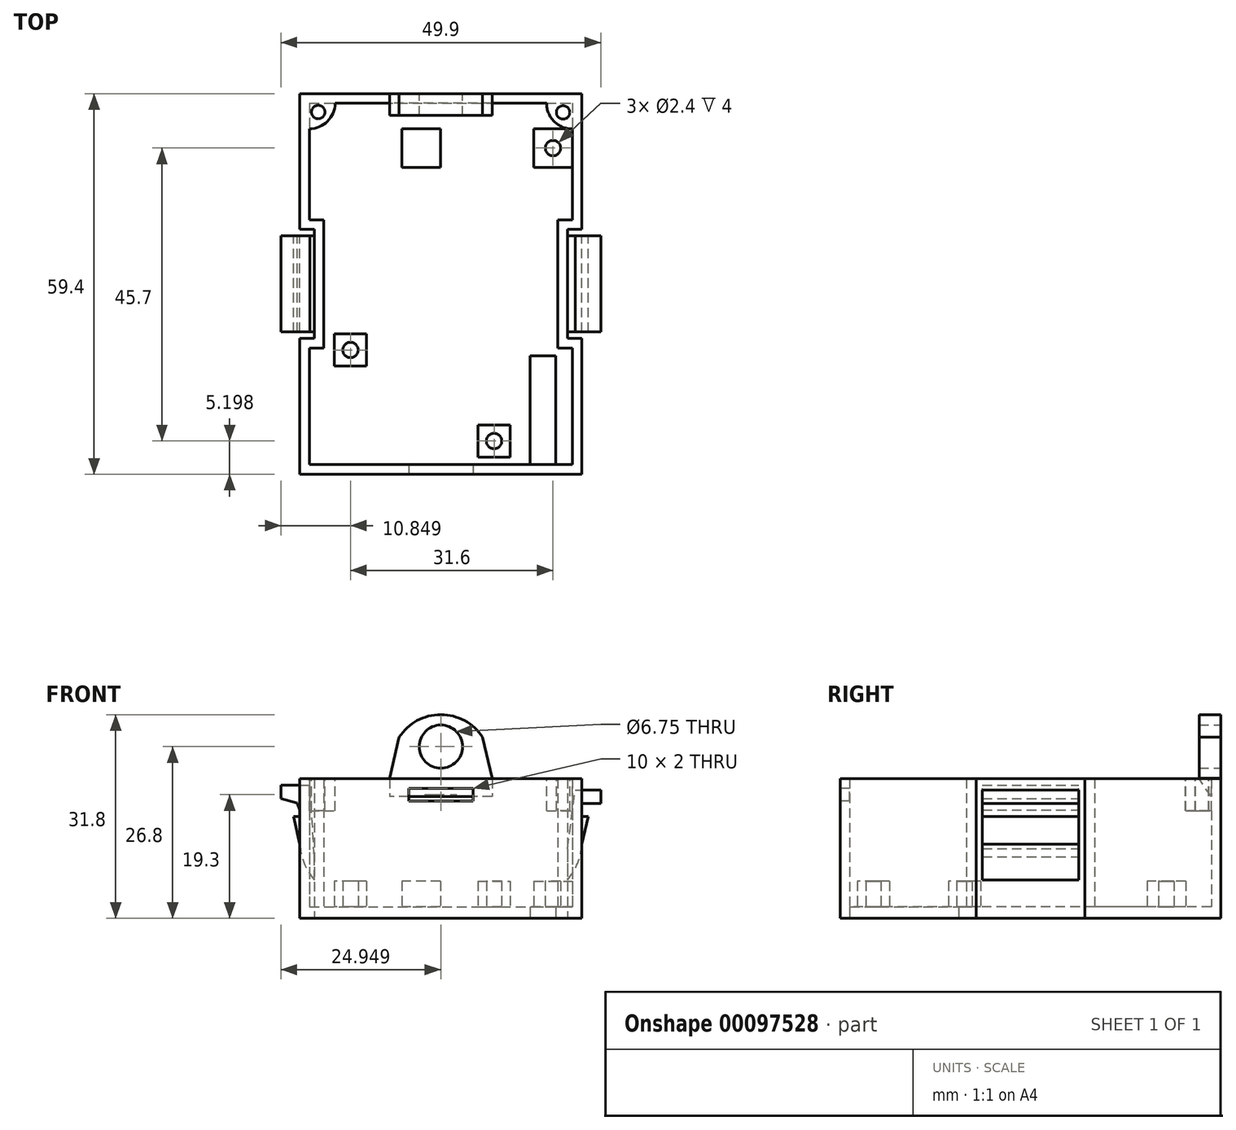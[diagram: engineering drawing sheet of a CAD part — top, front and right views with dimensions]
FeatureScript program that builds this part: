
annotation { "Feature Type Name" : "Feature", "Feature Type Description" : "" }
export const myFeature = defineFeature(function(context is Context, id is Id, definition is map)
    precondition{}
    {
        {
            var Q0;
            Q0=qCreatedBy(makeId("Top.planeOp"),FACE);
            var sketch = newSketch(context, id + "F0", { "sketchPlane" : qUnion([Q0])});
            skLineSegment(sketch, "E0.bottom", {"start": v(-56.63, 54.28) * mm, "end": v(-12.63, 54.28) * mm});
            skLineSegment(sketch, "E0.top", {"start": v(-56.63, -5.12) * mm, "end": v(-12.63, -5.12) * mm});
            skCircle(sketch, "E1", {"center": v(-12.63, -5.12) * mm, "radius": 1.5 * mm, "construction": true});
            skCircle(sketch, "E2", {"center": v(-56.63, -5.12) * mm, "radius": 1.5 * mm, "construction": true});
            skLineSegment(sketch, "E3", {"start": v(-56.63, -3.62) * mm, "end": v(-12.63, -3.62) * mm, "construction": true});
            skCircle(sketch, "E4", {"center": v(-12.63, -3.62) * mm, "radius": 4.1 * mm, "construction": true});
            skLineSegment(sketch, "E5.bottom", {"start": v(-16.73, -3.62) * mm, "end": v(-20.73, -3.62) * mm});
            skLineSegment(sketch, "E5.top", {"start": v(-16.73, 13.38) * mm, "end": v(-20.73, 13.38) * mm});
            skLineSegment(sketch, "E5.left", {"start": v(-16.73, -3.62) * mm, "end": v(-16.73, 13.38) * mm});
            skLineSegment(sketch, "E5.right", {"start": v(-20.73, -3.62) * mm, "end": v(-20.73, 13.38) * mm});
            skLineSegment(sketch, "E6", {"start": v(-56.63, 24.58) * mm, "end": v(-12.63, 24.58) * mm, "construction": true});
            skCircle(sketch, "E7", {"center": v(-56.63, 24.58) * mm, "radius": 8.5 * mm, "construction": true});
            skLineSegment(sketch, "E8", {"start": v(-56.63, 33.08) * mm, "end": v(-54.38, 33.08) * mm});
            skLineSegment(sketch, "E9", {"start": v(-56.63, 16.08) * mm, "end": v(-54.38, 16.08) * mm});
            skLineSegment(sketch, "E10", {"start": v(-54.38, 33.08) * mm, "end": v(-54.38, 16.08) * mm});
            skLineSegment(sketch, "E11", {"start": v(-56.63, 54.28) * mm, "end": v(-56.63, 33.08) * mm});
            skLineSegment(sketch, "E12", {"start": v(-56.63, 16.08) * mm, "end": v(-56.63, -5.12) * mm});
            skLineSegment(sketch, "E13", {"start": v(-34.63, 54.28) * mm, "end": v(-34.63, 40.65) * mm, "construction": true});
            skLineSegment(sketch, "E14.MirrorCS", {"start": v(-12.63, 16.08) * mm, "end": v(-12.63, -5.12) * mm});
            skLineSegment(sketch, "E15.MirrorCS", {"start": v(-12.63, 16.08) * mm, "end": v(-14.88, 16.08) * mm});
            skLineSegment(sketch, "E16.MirrorCS", {"start": v(-12.63, 33.08) * mm, "end": v(-14.88, 33.08) * mm});
            skLineSegment(sketch, "E17.MirrorCS", {"start": v(-12.63, 54.28) * mm, "end": v(-12.63, 33.08) * mm});
            skLineSegment(sketch, "E18.MirrorCS", {"start": v(-14.88, 33.08) * mm, "end": v(-14.88, 16.08) * mm});
            skSolve(sketch);
        }
        {
            var Q0;
            Q0=makeQuery(id+"F0.imprint","IMPRINT",FACE,{"disambiguationData":[TD([[makeQuery(id+"F0.imprint","IMPRINT",EDGE,{"derivedFrom":sQuery(id+"F0.wireOp",EDGE,"E0.bottom")}),-1.0]])]});
            extrude(context, id + "F1", {"entities" : qUnion([Q0]), "depth" : 1.8 * mm});
        }
        {
            var Q0;
            Q0=makeQuery(id+"F1.opExtrude","CAP_FACE",FACE,{"disambiguationData":[OSD([sQuery(id+"F0.wireOp",EDGE,"E0.bottom"),sQuery(id+"F0.wireOp",EDGE,"E0.top"),sQuery(id+"F0.wireOp",EDGE,"E5.bottom"),sQuery(id+"F0.wireOp",EDGE,"E5.top"),sQuery(id+"F0.wireOp",EDGE,"E5.left"),sQuery(id+"F0.wireOp",EDGE,"E5.right"),sQuery(id+"F0.wireOp",EDGE,"E8"),sQuery(id+"F0.wireOp",EDGE,"E9"),sQuery(id+"F0.wireOp",EDGE,"E10"),sQuery(id+"F0.wireOp",EDGE,"E11"),sQuery(id+"F0.wireOp",EDGE,"E12"),sQuery(id+"F0.wireOp",EDGE,"E14.MirrorCS"),sQuery(id+"F0.wireOp",EDGE,"E15.MirrorCS"),sQuery(id+"F0.wireOp",EDGE,"E16.MirrorCS"),sQuery(id+"F0.wireOp",EDGE,"E17.MirrorCS"),sQuery(id+"F0.wireOp",EDGE,"E18.MirrorCS")])],"isStart":false});
            var sketch = newSketch(context, id + "F2", { "sketchPlane" : qUnion([Q0])});
            skLineSegment(sketch, "E19.0", {"start": v(-55.13, 52.78) * mm, "end": v(-55.13, 34.58) * mm});
            skLineSegment(sketch, "E19.1", {"start": v(-14.13, 14.58) * mm, "end": v(-16.38, 14.58) * mm});
            skLineSegment(sketch, "E19.2", {"start": v(-16.38, 34.58) * mm, "end": v(-16.38, 14.58) * mm});
            skLineSegment(sketch, "E19.3", {"start": v(-14.13, 34.58) * mm, "end": v(-16.38, 34.58) * mm});
            skLineSegment(sketch, "E19.4", {"start": v(-14.13, 52.78) * mm, "end": v(-14.13, 34.58) * mm});
            skLineSegment(sketch, "E19.5", {"start": v(-14.13, 14.58) * mm, "end": v(-14.13, -3.62) * mm});
            skLineSegment(sketch, "E19.6", {"start": v(-55.13, 52.78) * mm, "end": v(-14.13, 52.78) * mm});
            skLineSegment(sketch, "E19.7", {"start": v(-55.13, -3.62) * mm, "end": v(-14.13, -3.62) * mm});
            skLineSegment(sketch, "E19.8", {"start": v(-55.13, 14.58) * mm, "end": v(-55.13, -3.62) * mm});
            skLineSegment(sketch, "E19.9", {"start": v(-55.13, 14.58) * mm, "end": v(-52.88, 14.58) * mm});
            skLineSegment(sketch, "E19.10", {"start": v(-52.88, 34.58) * mm, "end": v(-52.88, 14.58) * mm});
            skLineSegment(sketch, "E19.11", {"start": v(-55.13, 34.58) * mm, "end": v(-52.88, 34.58) * mm});
            skSolve(sketch);
        }
        {
            var Q0;
            Q0=makeQuery(id+"F2.imprint","IMPRINT",FACE,{"disambiguationData":[TD([[makeQuery(id+"F2.imprint","IMPRINT",EDGE,{"derivedFrom":sQuery(id+"F2.wireOp",EDGE,"E19.0")}),-1.0]])]});
            extrude(context, id + "F3", {"entities" : qUnion([Q0]), "operationType" : NewBodyOperationType.ADD, "depth" : 20 * mm});
        }
        {
            var Q0;
            {var subQ0=sQuery(id+"F0.wireOp",EDGE,"E8");Q0=makeQuery(id+"F3.boolean.opBoolean","MERGE",FACE,{"derivedFrom":[makeQuery(id+"F1.opExtrude","SWEPT_FACE",FACE,{"disambiguationData":[OSD([subQ0])]}),makeQuery(id+"F3.opExtrude","SWEPT_FACE",FACE,{"disambiguationData":[OSD([subQ0])]})]});}
            var sketch = newSketch(context, id + "F4", { "sketchPlane" : qUnion([Q0])});
            skLineSegment(sketch, "E20", {"start": v(-56.63, 21.8) * mm, "end": v(-54.38, 21.8) * mm});
            skLineSegment(sketch, "E21", {"start": v(-56.63, 21.8) * mm, "end": v(-56.63, 22.8) * mm});
            skLineSegment(sketch, "E22", {"start": v(-56.63, 21.8) * mm, "end": v(-55.5, 21.8) * mm});
            skCircle(sketch, "E23", {"center": v(-56.63, 21.8) * mm, "radius": 2 * mm, "construction": true});
            skLineSegment(sketch, "E24", {"start": v(-56.63, 22.8) * mm, "end": v(-54.38, 21.8) * mm});
            skSolve(sketch);
        }
        {
            var Q0;
            Q0=qSketchRegion(id+"F4",true);
            extrude(context, id + "F5", {"entities" : qUnion([Q0]), "operationType" : NewBodyOperationType.REMOVE, "depth" : 17 * mm});
        }
        {
            var Q0;
            {var subQ0=sQuery(id+"F0.wireOp",EDGE,"E15.MirrorCS");Q0=makeQuery(id+"F3.boolean.opBoolean","MERGE",FACE,{"derivedFrom":[makeQuery(id+"F1.opExtrude","SWEPT_FACE",FACE,{"disambiguationData":[OSD([subQ0])]}),makeQuery(id+"F3.opExtrude","SWEPT_FACE",FACE,{"disambiguationData":[OSD([subQ0])]})]});}
            var sketch = newSketch(context, id + "F6", { "sketchPlane" : qUnion([Q0])});
            skLineSegment(sketch, "E25", {"start": v(12.63, 21.8) * mm, "end": v(12.63, 22.8) * mm});
            skLineSegment(sketch, "E26", {"start": v(12.63, 22.8) * mm, "end": v(14.88, 21.8) * mm});
            skLineSegment(sketch, "E27", {"start": v(14.88, 21.8) * mm, "end": v(12.63, 21.8) * mm});
            skSolve(sketch);
        }
        {
            var Q0;
            Q0=qSketchRegion(id+"F6",true);
            extrude(context, id + "F7", {"entities" : qUnion([Q0]), "operationType" : NewBodyOperationType.REMOVE, "depth" : 17 * mm});
        }
        {
            var Q0;
            {var subQ0=sQuery(id+"F0.wireOp",EDGE,"E0.top");Q0=makeQuery(id+"F6ghHVKL5EjysOi_1.boolean.opBoolean","MERGE",FACE,{"derivedFrom":[makeQuery(id+"F3.boolean.opBoolean","MERGE",FACE,{"derivedFrom":[makeQuery(id+"F1.opExtrude","SWEPT_FACE",FACE,{"disambiguationData":[OSD([subQ0])]}),makeQuery(id+"F3.opExtrude","SWEPT_FACE",FACE,{"disambiguationData":[OSD([subQ0])]})]}),makeQuery(id+"F6ghHVKL5EjysOi_1.opExtrude","SWEPT_FACE",FACE,{"disambiguationData":[OSD([sQuery(id+"FZ5MUIDVzBKq7bX_1.wireOp",EDGE,"YdwC2A8M-5GiA-6Idz-uFSA-seqV52Q8DN6U.top")])]})]});}
            var sketch = newSketch(context, id + "F8", { "sketchPlane" : qUnion([Q0])});
            skLineSegment(sketch, "E28.top", {"start": v(-29.63, 21.8) * mm, "end": v(-39.63, 21.8) * mm});
            skCircle(sketch, "E29", {"center": v(-56.63, 21.8) * mm, "radius": 1.5 * mm, "construction": true});
            skLineSegment(sketch, "E30", {"start": v(-56.63, 20.3) * mm, "end": v(-12.63, 20.3) * mm, "construction": true});
            skCircle(sketch, "E31", {"center": v(-34.63, 20.3) * mm, "radius": 5 * mm, "construction": true});
            skLineSegment(sketch, "E32", {"start": v(-39.63, 20.3) * mm, "end": v(-39.63, 18.3) * mm, "construction": true});
            skLineSegment(sketch, "E33.bottom", {"start": v(-39.63, 18.3) * mm, "end": v(-29.63, 18.3) * mm});
            skLineSegment(sketch, "E33.top", {"start": v(-39.63, 20.3) * mm, "end": v(-29.63, 20.3) * mm});
            skLineSegment(sketch, "E33.left", {"start": v(-39.63, 18.3) * mm, "end": v(-39.63, 20.3) * mm});
            skLineSegment(sketch, "E33.right", {"start": v(-29.63, 18.3) * mm, "end": v(-29.63, 20.3) * mm});
            skSolve(sketch);
        }
        {
            var Q0;
            Q0=qSketchRegion(id+"F8",true);
            extrude(context, id + "F9", {"entities" : qUnion([Q0]), "operationType" : NewBodyOperationType.REMOVE, "oppositeDirection" : true, "depth" : 2.5 * mm});
        }
        {
            var Q0;
            {var subQ0=sQuery(id+"F0.wireOp",EDGE,"E16.MirrorCS");Q0=makeQuery(id+"F7.boolean.opBoolean","MERGE",FACE,{"derivedFrom":[makeQuery(id+"F3.boolean.opBoolean","MERGE",FACE,{"derivedFrom":[makeQuery(id+"F1.opExtrude","SWEPT_FACE",FACE,{"disambiguationData":[OSD([subQ0])]}),makeQuery(id+"F3.opExtrude","SWEPT_FACE",FACE,{"disambiguationData":[OSD([subQ0])]})]}),makeQuery(id+"F7.opExtrude","CAP_FACE",FACE,{"disambiguationData":[OSD([sQuery(id+"F6.wireOp",EDGE,"E25"),sQuery(id+"F6.wireOp",EDGE,"E26"),sQuery(id+"F6.wireOp",EDGE,"E27")])],"isStart":false})]});}
            var sketch = newSketch(context, id + "F10", { "sketchPlane" : qUnion([Q0])});
            skLineSegment(sketch, "E34", {"start": v(-14.88, 0) * mm, "end": v(-14.88, 6) * mm, "construction": true});
            skCircle(sketch, "E35", {"center": v(-14.88, 6) * mm, "radius": 6 * mm, "construction": true});
            skArc(sketch, "E36", {"start": v(-14.88, 6) * mm, "mid": v(-13.3, 8.6) * mm, "end": v(-12.63, 11.56) * mm});
            skCircle(sketch, "E37", {"center": v(-14.88, 10.9) * mm, "radius": 5 * mm, "construction": true});
            skLineSegment(sketch, "E38", {"start": v(-14.88, 15.9) * mm, "end": v(-5.95, 15.9) * mm, "construction": true});
            skCircle(sketch, "E39", {"center": v(-12.63, 15.9) * mm, "radius": 1 * mm, "construction": true});
            skLineSegment(sketch, "E40", {"start": v(-12.63, 11.56) * mm, "end": v(-11.63, 15.9) * mm});
            skCircle(sketch, "E41", {"center": v(-14.88, 15.9) * mm, "radius": 1.2 * mm, "construction": true});
            skLineSegment(sketch, "E42", {"start": v(-13.68, 20) * mm, "end": v(-9.68, 20) * mm});
            skLineSegment(sketch, "E43", {"start": v(-11.63, 15.9) * mm, "end": v(-12.63, 15.9) * mm});
            skCircle(sketch, "E44", {"center": v(-12.63, 15.9) * mm, "radius": 2 * mm, "construction": true});
            skLineSegment(sketch, "E45", {"start": v(-12.63, 15.9) * mm, "end": v(-12.63, 17.9) * mm});
            skLineSegment(sketch, "E46", {"start": v(-12.63, 17.9) * mm, "end": v(-9.68, 17.9) * mm});
            skLineSegment(sketch, "E47", {"start": v(-14.88, 10.9) * mm, "end": v(-13.68, 20) * mm});
            skLineSegment(sketch, "E48", {"start": v(-9.68, 20) * mm, "end": v(-9.68, 17.9) * mm});
            skLineSegment(sketch, "E49", {"start": v(-12.63, 6.02) * mm, "end": v(-56.63, 6.02) * mm, "construction": true});
            skLineSegment(sketch, "E50", {"start": v(-34.63, 6.02) * mm, "end": v(-34.63, 12.32) * mm, "construction": true});
            skCircle(sketch, "E51.MirrorC", {"center": v(-56.63, 15.9) * mm, "radius": 2 * mm, "construction": true});
            skLineSegment(sketch, "E52.MirrorCS", {"start": v(-56.63, 11.56) * mm, "end": v(-57.63, 15.9) * mm});
            skArc(sketch, "E53.MirrorCS", {"start": v(-54.38, 6) * mm, "mid": v(-55.96, 8.6) * mm, "end": v(-56.63, 11.56) * mm});
            skLineSegment(sketch, "E54.MirrorCS", {"start": v(-57.63, 15.9) * mm, "end": v(-56.63, 15.9) * mm});
            skLineSegment(sketch, "E55", {"start": v(-14.88, 10.9) * mm, "end": v(-14.88, 6) * mm});
            skCircle(sketch, "E56", {"center": v(-56.63, 17.9) * mm, "radius": 0.8 * mm, "construction": true});
            skPoint(sketch, "E57.endSnap0", {"position": v(-56.63, 16.9) * mm});
            skLineSegment(sketch, "E58", {"start": v(-56.63, 18.7) * mm, "end": v(-59.88, 18.7) * mm, "construction": true});
            skLineSegment(sketch, "E59", {"start": v(-59.58, 18.7) * mm, "end": v(-59.58, 20.8) * mm});
            skLineSegment(sketch, "E60", {"start": v(-59.58, 18.7) * mm, "end": v(-57.03, 18) * mm});
            skLineSegment(sketch, "E61", {"start": v(-56.63, 15.9) * mm, "end": v(-56.63, 16.9) * mm});
            skLineSegment(sketch, "E62", {"start": v(-56.63, 16.9) * mm, "end": v(-57.03, 18) * mm});
            skLineSegment(sketch, "E63", {"start": v(-59.58, 20.8) * mm, "end": v(-55.04, 20.8) * mm});
            skLineSegment(sketch, "E64", {"start": v(-54.38, 6) * mm, "end": v(-54.38, 9.6) * mm});
            skLineSegment(sketch, "E65", {"start": v(-54.38, 9.6) * mm, "end": v(-55.04, 20.8) * mm});
            skSolve(sketch);
        }
        {
            var Q0;
            Q0=makeQuery(id+"F10.imprint","IMPRINT",FACE,{"disambiguationData":[TD([[makeQuery(id+"F10.imprint","IMPRINT",EDGE,{"derivedFrom":sQuery(id+"F10.wireOp",EDGE,"3a5f83b2-c532-4f29-86cb-ad45a0fee2c30.MirrorCS")}),1.0]])]});
            var Q1;
            {var subQ6=sQuery(id+"F10.wireOp",EDGE,"E46");Q1=makeQuery(id+"F10.imprint","IMPRINT",FACE,{"disambiguationData":[TD([[makeQuery(id+"F10.imprint","IMPRINT",EDGE,{"derivedFrom":subQ6}),1.0]])]});}
            var Q2;
            {var subQ7=sQuery(id+"F10.wireOp",EDGE,"E36");Q2=makeQuery(id+"F10.imprint","IMPRINT",FACE,{"disambiguationData":[TD([[makeQuery(id+"F10.imprint","IMPRINT",EDGE,{"derivedFrom":subQ7}),1.0]])]});}
            var Q3;
            {var subQ0=sQuery(id+"F10.wireOp",EDGE,"E40");Q3=makeQuery(id+"F10.imprint","IMPRINT",FACE,{"disambiguationData":[TD([[makeQuery(id+"F10.imprint","IMPRINT",EDGE,{"derivedFrom":subQ0}),1.0]])]});}
            var Q4;
            Q4=makeQuery(id+"F10.imprint","IMPRINT",FACE,{"disambiguationData":[TD([[makeQuery(id+"F10.imprint","IMPRINT",EDGE,{"derivedFrom":sQuery(id+"F10.wireOp",EDGE,"E52.MirrorCS")}),-1.0]])]});
            extrude(context, id + "F11", {"entities" : qUnion([Q0, Q1, Q2, Q3, Q4]), "operationType" : NewBodyOperationType.ADD, "depth" : 16 * mm, "hasSecondDirection" : true, "secondDirectionOppositeDirection" : false, "secondDirectionDepth" : 1 * mm});
        }
        {
            var Q0;
            Q0=makeQuery(id+"F1.opExtrude","CAP_FACE",FACE,{"disambiguationData":[OSD([sQuery(id+"F0.wireOp",EDGE,"E0.bottom"),sQuery(id+"F0.wireOp",EDGE,"E0.top"),sQuery(id+"F0.wireOp",EDGE,"E5.bottom"),sQuery(id+"F0.wireOp",EDGE,"E5.top"),sQuery(id+"F0.wireOp",EDGE,"E5.left"),sQuery(id+"F0.wireOp",EDGE,"E5.right"),sQuery(id+"F0.wireOp",EDGE,"E8"),sQuery(id+"F0.wireOp",EDGE,"E9"),sQuery(id+"F0.wireOp",EDGE,"E10"),sQuery(id+"F0.wireOp",EDGE,"E11"),sQuery(id+"F0.wireOp",EDGE,"E12"),sQuery(id+"F0.wireOp",EDGE,"E14.MirrorCS"),sQuery(id+"F0.wireOp",EDGE,"E15.MirrorCS"),sQuery(id+"F0.wireOp",EDGE,"E16.MirrorCS"),sQuery(id+"F0.wireOp",EDGE,"E17.MirrorCS"),sQuery(id+"F0.wireOp",EDGE,"E18.MirrorCS")])],"isStart":false});
            var sketch = newSketch(context, id + "F12", { "sketchPlane" : qUnion([Q0])});
            skCircle(sketch, "E66", {"center": v(-14.13, 34.58) * mm, "radius": 3 * mm, "construction": true});
            skLineSegment(sketch, "E67", {"start": v(-14.13, 34.58) * mm, "end": v(-19.1, 34.58) * mm, "construction": true});
            skLineSegment(sketch, "E68", {"start": v(-17.13, 34.58) * mm, "end": v(-17.13, 52.78) * mm, "construction": true});
            skCircle(sketch, "E69", {"center": v(-17.13, 52.78) * mm, "radius": 7 * mm, "construction": true});
            skCircle(sketch, "E70", {"center": v(-17.13, 45.78) * mm, "radius": 3 * mm, "construction": true});
            skCircle(sketch, "E71", {"center": v(-17.13, 45.78) * mm, "radius": 1.2 * mm});
            skLineSegment(sketch, "E72.bottom", {"start": v(-20.13, 48.78) * mm, "end": v(-14.13, 48.78) * mm});
            skLineSegment(sketch, "E72.top", {"start": v(-20.13, 42.78) * mm, "end": v(-14.13, 42.78) * mm});
            skLineSegment(sketch, "E72.left", {"start": v(-20.13, 48.78) * mm, "end": v(-20.13, 42.78) * mm});
            skLineSegment(sketch, "E72.right", {"start": v(-14.13, 48.78) * mm, "end": v(-14.13, 42.78) * mm});
            skLineSegment(sketch, "E73", {"start": v(-49.88, -3.62) * mm, "end": v(-49.88, 0.08) * mm, "construction": true});
            skLineSegment(sketch, "E74", {"start": v(-49.88, 0.08) * mm, "end": v(-11.04, 0.08) * mm, "construction": true});
            skCircle(sketch, "E75", {"center": v(-14.13, 0.08) * mm, "radius": 12.2 * mm, "construction": true});
            skCircle(sketch, "E76", {"center": v(-26.33, 0.08) * mm, "radius": 1.2 * mm});
            skLineSegment(sketch, "E77.bottom", {"start": v(-28.83, 2.58) * mm, "end": v(-23.83, 2.58) * mm});
            skLineSegment(sketch, "E77.top", {"start": v(-28.83, -2.42) * mm, "end": v(-23.83, -2.42) * mm});
            skLineSegment(sketch, "E77.left", {"start": v(-28.83, 2.58) * mm, "end": v(-28.83, -2.42) * mm});
            skLineSegment(sketch, "E77.right", {"start": v(-23.83, 2.58) * mm, "end": v(-23.83, -2.42) * mm});
            skLineSegment(sketch, "E78", {"start": v(-55.13, -2.16) * mm, "end": v(-48.73, -2.16) * mm, "construction": true});
            skLineSegment(sketch, "E79", {"start": v(-48.73, -2.16) * mm, "end": v(-48.73, 60.43) * mm, "construction": true});
            skLineSegment(sketch, "E80", {"start": v(-48.73, -2.16) * mm, "end": v(-48.73, -6.57) * mm, "construction": true});
            skCircle(sketch, "E81", {"center": v(-48.73, -3.62) * mm, "radius": 17.9 * mm, "construction": true});
            skCircle(sketch, "E82", {"center": v(-48.73, 14.28) * mm, "radius": 1.2 * mm});
            skLineSegment(sketch, "E83.bottom", {"start": v(-46.23, 16.78) * mm, "end": v(-51.23, 16.78) * mm});
            skLineSegment(sketch, "E83.top", {"start": v(-46.23, 11.78) * mm, "end": v(-51.23, 11.78) * mm});
            skLineSegment(sketch, "E83.left", {"start": v(-46.23, 16.78) * mm, "end": v(-46.23, 11.78) * mm});
            skLineSegment(sketch, "E83.right", {"start": v(-51.23, 16.78) * mm, "end": v(-51.23, 11.78) * mm});
            skLineSegment(sketch, "E84", {"start": v(-17.13, 45.78) * mm, "end": v(-37.7, 45.78) * mm, "construction": true});
            skLineSegment(sketch, "E85.bottom", {"start": v(-34.7, 48.78) * mm, "end": v(-40.7, 48.78) * mm});
            skLineSegment(sketch, "E85.top", {"start": v(-34.7, 42.78) * mm, "end": v(-40.7, 42.78) * mm});
            skLineSegment(sketch, "E85.left", {"start": v(-34.7, 48.78) * mm, "end": v(-34.7, 42.78) * mm});
            skLineSegment(sketch, "E85.right", {"start": v(-40.7, 48.78) * mm, "end": v(-40.7, 42.78) * mm});
            skPoint(sketch, "E85.middle", {"position": v(-37.7, 45.78) * mm});
            skSolve(sketch);
        }
        {
            var Q0;
            Q0=makeQuery(id+"F12.imprint","IMPRINT",FACE,{"disambiguationData":[TD([[makeQuery(id+"F12.imprint","IMPRINT",EDGE,{"derivedFrom":sQuery(id+"F12.wireOp",EDGE,"E82")}),-1.0]])]});
            var Q1;
            Q1=makeQuery(id+"F12.imprint","IMPRINT",FACE,{"disambiguationData":[TD([[makeQuery(id+"F12.imprint","IMPRINT",EDGE,{"derivedFrom":sQuery(id+"F12.wireOp",EDGE,"E76")}),-1.0]])]});
            var Q2;
            Q2=makeQuery(id+"F12.imprint","IMPRINT",FACE,{"disambiguationData":[TD([[makeQuery(id+"F12.imprint","IMPRINT",EDGE,{"derivedFrom":sQuery(id+"F12.wireOp",EDGE,"E71")}),-1.0]])]});
            var Q3;
            Q3=makeQuery(id+"F12.imprint","IMPRINT",FACE,{"disambiguationData":[TD([[makeQuery(id+"F12.imprint","IMPRINT",EDGE,{"derivedFrom":sQuery(id+"F12.wireOp",EDGE,"E85.bottom")}),1.0]])]});
            extrude(context, id + "F13", {"entities" : qUnion([Q0, Q1, Q2, Q3]), "operationType" : NewBodyOperationType.ADD, "depth" : 4 * mm});
        }
        {
            var Q0;
            Q0=makeQuery(id+"F3.opExtrude","CAP_FACE",FACE,{"disambiguationData":[OSD([sQuery(id+"F0.wireOp",EDGE,"E0.bottom"),sQuery(id+"F0.wireOp",EDGE,"E0.top"),sQuery(id+"F0.wireOp",EDGE,"E8"),sQuery(id+"F0.wireOp",EDGE,"E9"),sQuery(id+"F0.wireOp",EDGE,"E10"),sQuery(id+"F0.wireOp",EDGE,"E11"),sQuery(id+"F0.wireOp",EDGE,"E12"),sQuery(id+"F0.wireOp",EDGE,"E14.MirrorCS"),sQuery(id+"F0.wireOp",EDGE,"E15.MirrorCS"),sQuery(id+"F0.wireOp",EDGE,"E16.MirrorCS"),sQuery(id+"F0.wireOp",EDGE,"E17.MirrorCS"),sQuery(id+"F0.wireOp",EDGE,"E18.MirrorCS"),sQuery(id+"F2.wireOp",EDGE,"E19.0"),sQuery(id+"F2.wireOp",EDGE,"E19.1"),sQuery(id+"F2.wireOp",EDGE,"E19.2"),sQuery(id+"F2.wireOp",EDGE,"E19.3"),sQuery(id+"F2.wireOp",EDGE,"E19.4"),sQuery(id+"F2.wireOp",EDGE,"E19.5"),sQuery(id+"F2.wireOp",EDGE,"E19.6"),sQuery(id+"F2.wireOp",EDGE,"E19.7"),sQuery(id+"F2.wireOp",EDGE,"E19.8"),sQuery(id+"F2.wireOp",EDGE,"E19.9"),sQuery(id+"F2.wireOp",EDGE,"E19.10"),sQuery(id+"F2.wireOp",EDGE,"E19.11")])],"isStart":false});
            var sketch = newSketch(context, id + "F14", { "sketchPlane" : qUnion([Q0])});
            skCircle(sketch, "E86", {"center": v(-55.13, 52.78) * mm, "radius": 4 * mm, "construction": true});
            skArc(sketch, "E87", {"start": v(-55.13, 48.78) * mm, "mid": v(-52.32, 49.97) * mm, "end": v(-51.13, 52.78) * mm});
            skLineSegment(sketch, "E88", {"start": v(-55.19, 52.83) * mm, "end": v(-52.32, 49.97) * mm, "construction": true});
            skCircle(sketch, "E89", {"center": v(-53.75, 51.4) * mm, "radius": 1.05 * mm});
            skCircle(sketch, "E90", {"center": v(-14.13, 52.78) * mm, "radius": 4 * mm, "construction": true});
            skArc(sketch, "E91", {"start": v(-18.13, 52.78) * mm, "mid": v(-16.97, 49.94) * mm, "end": v(-14.13, 48.78) * mm});
            skLineSegment(sketch, "E92", {"start": v(-14.16, 52.75) * mm, "end": v(-16.97, 49.94) * mm, "construction": true});
            skCircle(sketch, "E93", {"center": v(-15.56, 51.35) * mm, "radius": 1.05 * mm});
            skLineSegment(sketch, "E94", {"start": v(-55.13, 48.78) * mm, "end": v(-55.13, 52.78) * mm});
            skLineSegment(sketch, "E95", {"start": v(-18.13, 52.78) * mm, "end": v(-14.13, 52.78) * mm});
            skLineSegment(sketch, "E96", {"start": v(-51.13, 52.78) * mm, "end": v(-18.13, 52.78) * mm});
            skLineSegment(sketch, "E97", {"start": v(-14.13, 48.78) * mm, "end": v(-14.13, 34.58) * mm});
            skLineSegment(sketch, "E98", {"start": v(-14.13, 34.58) * mm, "end": v(-16.38, 34.58) * mm});
            skLineSegment(sketch, "E99", {"start": v(-16.38, 34.58) * mm, "end": v(-16.38, 14.58) * mm});
            skLineSegment(sketch, "E100", {"start": v(-16.38, 14.58) * mm, "end": v(-14.13, 14.58) * mm});
            skLineSegment(sketch, "E101", {"start": v(-14.13, 14.58) * mm, "end": v(-14.13, -3.62) * mm});
            skLineSegment(sketch, "E102", {"start": v(-14.13, -3.62) * mm, "end": v(-55.13, -3.62) * mm});
            skLineSegment(sketch, "E103", {"start": v(-55.13, -3.62) * mm, "end": v(-55.13, 14.58) * mm});
            skLineSegment(sketch, "E104", {"start": v(-55.13, 14.58) * mm, "end": v(-52.88, 14.58) * mm});
            skLineSegment(sketch, "E105", {"start": v(-52.88, 14.58) * mm, "end": v(-52.88, 34.58) * mm});
            skLineSegment(sketch, "E106", {"start": v(-52.88, 34.58) * mm, "end": v(-55.13, 34.58) * mm});
            skLineSegment(sketch, "E107", {"start": v(-55.13, 34.58) * mm, "end": v(-55.13, 48.78) * mm});
            skLineSegment(sketch, "E108", {"start": v(-51.13, 52.78) * mm, "end": v(-55.13, 52.78) * mm});
            skSolve(sketch);
        }
        {
            var Q0;
            Q0=makeQuery(id+"F14.imprint","IMPRINT",FACE,{"disambiguationData":[TD([[makeQuery(id+"F14.imprint","IMPRINT",EDGE,{"derivedFrom":sQuery(id+"F14.wireOp",EDGE,"E93")}),-1.0]])]});
            var Q1;
            Q1=makeQuery(id+"F14.imprint","IMPRINT",FACE,{"disambiguationData":[TD([[makeQuery(id+"F14.imprint","IMPRINT",EDGE,{"derivedFrom":sQuery(id+"F14.wireOp",EDGE,"E89")}),-1.0]])]});
            extrude(context, id + "F15", {"entities" : qUnion([Q0, Q1]), "operationType" : NewBodyOperationType.ADD, "oppositeDirection" : true, "depth" : 5 * mm});
        }
        {
            var Q0;
            {var subQ0=sQuery(id+"F0.wireOp",EDGE,"E0.bottom");Q0=makeQuery(id+"F3.boolean.opBoolean","MERGE",FACE,{"derivedFrom":[makeQuery(id+"F1.opExtrude","SWEPT_FACE",FACE,{"disambiguationData":[OSD([subQ0])]}),makeQuery(id+"F3.opExtrude","SWEPT_FACE",FACE,{"disambiguationData":[OSD([subQ0])]})]});}
            var sketch = newSketch(context, id + "F16", { "sketchPlane" : qUnion([Q0])});
            skLineSegment(sketch, "E109", {"start": v(34.63, 21.8) * mm, "end": v(34.63, 31.8) * mm, "construction": true});
            skCircle(sketch, "E110", {"center": v(34.63, 26.8) * mm, "radius": 3.38 * mm});
            skCircle(sketch, "E111", {"center": v(34.63, 26.8) * mm, "radius": 5 * mm, "construction": true});
            skLineSegment(sketch, "E112", {"start": v(29.85, 28.25) * mm, "end": v(39.42, 28.25) * mm, "construction": true});
            skArc(sketch, "E113", {"start": v(39.42, 28.25) * mm, "mid": v(34.63, 31.8) * mm, "end": v(29.85, 28.25) * mm});
            skLineSegment(sketch, "E114", {"start": v(34.63, 28.25) * mm, "end": v(28.13, 28.25) * mm, "construction": true});
            skLineSegment(sketch, "E115", {"start": v(34.63, 28.25) * mm, "end": v(41.13, 28.25) * mm, "construction": true});
            skArc(sketch, "E116", {"start": v(41.13, 28.25) * mm, "mid": v(34.63, 31.8) * mm, "end": v(28.13, 28.25) * mm});
            skCircle(sketch, "E117", {"center": v(34.63, 21.8) * mm, "radius": 8 * mm, "construction": true});
            skLineSegment(sketch, "E118", {"start": v(42.63, 21.8) * mm, "end": v(42.63, 21.9) * mm});
            skLineSegment(sketch, "E119", {"start": v(26.63, 21.8) * mm, "end": v(26.63, 21.9) * mm});
            skLineSegment(sketch, "E120", {"start": v(26.63, 21.9) * mm, "end": v(28.13, 28.25) * mm});
            skLineSegment(sketch, "E121", {"start": v(42.63, 21.9) * mm, "end": v(41.13, 28.25) * mm});
            skSolve(sketch);
        }
        {
            var Q0;
            Q0=makeQuery(id+"F16.imprint","IMPRINT",FACE,{"disambiguationData":[TD([[makeQuery(id+"F16.imprint","IMPRINT",EDGE,{"derivedFrom":sQuery(id+"F16.wireOp",EDGE,"E110")}),-1.0]])]});
            extrude(context, id + "F17", {"entities" : qUnion([Q0]), "operationType" : NewBodyOperationType.ADD, "oppositeDirection" : true, "depth" : 3.4 * mm});
        }
        {
            var Q0;
            Q0=makeQuery(id+"F17.opExtrude","SWEPT_FACE",FACE,{"disambiguationData":[OSD([sQuery(id+"F16.wireOp",EDGE,"E118")])]});
            var sketch = newSketch(context, id + "F18", { "sketchPlane" : qUnion([Q0])});
            skLineSegment(sketch, "E122", {"start": v(-52.78, 21.8) * mm, "end": v(-52.78, 18.99) * mm});
            skLineSegment(sketch, "E123", {"start": v(-52.78, 18.99) * mm, "end": v(-50.88, 21.8) * mm});
            skLineSegment(sketch, "E124", {"start": v(-50.88, 21.8) * mm, "end": v(-52.78, 21.8) * mm});
            skSolve(sketch);
        }
        {
            var Q0;
            Q0=makeQuery(id+"F18.imprint","IMPRINT",FACE,{"disambiguationData":[TD([[makeQuery(id+"F18.imprint","IMPRINT",EDGE,{"derivedFrom":sQuery(id+"F18.wireOp",EDGE,"E122")}),1.0]])]});
            extrude(context, id + "F19", {"entities" : qUnion([Q0]), "operationType" : NewBodyOperationType.ADD, "oppositeDirection" : true, "depth" : 16 * mm});
        }
    });
